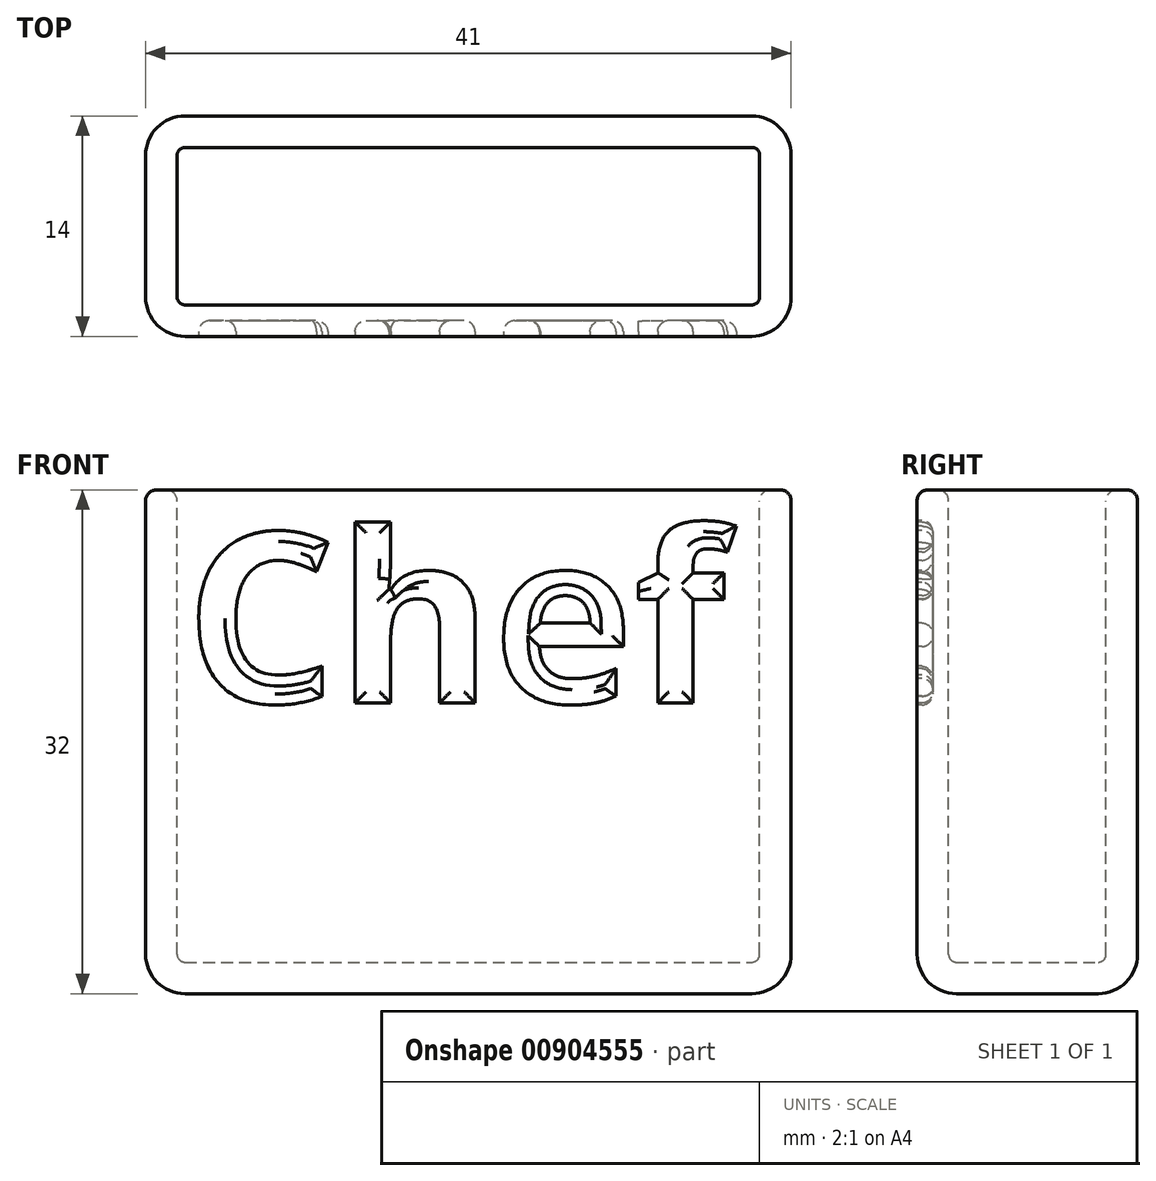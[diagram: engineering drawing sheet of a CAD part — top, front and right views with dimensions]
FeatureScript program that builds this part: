
annotation { "Feature Type Name" : "Feature", "Feature Type Description" : "" }
export const myFeature = defineFeature(function(context is Context, id is Id, definition is map)
    precondition{}
    {
        {
            var Q0;
            Q0=qCreatedBy(makeId("Top.planeOp"),FACE);
            var sketch = newSketch(context, id + "F0", { "sketchPlane" : qUnion([Q0])});
            skLineSegment(sketch, "E0.bottom", {"start": v(0, 0) * mm, "end": v(41, 0) * mm});
            skLineSegment(sketch, "E0.top", {"start": v(0, 14) * mm, "end": v(41, 14) * mm});
            skLineSegment(sketch, "E0.left", {"start": v(0, 0) * mm, "end": v(0, 14) * mm});
            skLineSegment(sketch, "E0.right", {"start": v(41, 0) * mm, "end": v(41, 14) * mm});
            skSolve(sketch);
        }
        {
            var Q0;
            Q0 = qSketchRegion(id + "F0", true);
            extrude(context, id + "F1", {"entities" : qUnion([Q0]), "depth" : 32 * mm, "offsetDistance" : 25 * mm});
        }
        {
            var Q0;
            Q0=makeQuery(id+"F1.opExtrude","SWEPT_EDGE",EDGE,{"disambiguationData":[OSD([sQuery(id+"F0.wireOp",EDGE,"E0.bottom"),sQuery(id+"F0.wireOp",EDGE,"E0.left")])]});
            var Q1;
            Q1=makeQuery(id+"F1.opExtrude","CAP_EDGE",EDGE,{"disambiguationData":[OSD([sQuery(id+"F0.wireOp",EDGE,"E0.bottom")])],"isStart":true});
            var Q2;
            Q2=makeQuery(id+"F1.opExtrude","SWEPT_EDGE",EDGE,{"disambiguationData":[OSD([sQuery(id+"F0.wireOp",EDGE,"E0.bottom"),sQuery(id+"F0.wireOp",EDGE,"E0.right")])]});
            var Q3;
            Q3=makeQuery(id+"F1.opExtrude","SWEPT_EDGE",EDGE,{"disambiguationData":[OSD([sQuery(id+"F0.wireOp",EDGE,"E0.top"),sQuery(id+"F0.wireOp",EDGE,"E0.right")])]});
            var Q4;
            Q4=makeQuery(id+"F1.opExtrude","SWEPT_EDGE",EDGE,{"disambiguationData":[OSD([sQuery(id+"F0.wireOp",EDGE,"E0.top"),sQuery(id+"F0.wireOp",EDGE,"E0.left")])]});
            var Q5;
            Q5=makeQuery(id+"F1.opExtrude","CAP_EDGE",EDGE,{"disambiguationData":[OSD([sQuery(id+"F0.wireOp",EDGE,"E0.top")])],"isStart":true});
            var Q6;
            Q6=makeQuery(id+"F1.opExtrude","CAP_EDGE",EDGE,{"disambiguationData":[OSD([sQuery(id+"F0.wireOp",EDGE,"E0.left")])],"isStart":true});
            var Q7;
            Q7=makeQuery(id+"F1.opExtrude","CAP_EDGE",EDGE,{"disambiguationData":[OSD([sQuery(id+"F0.wireOp",EDGE,"E0.right")])],"isStart":true});
            fillet(context, id + "F2", {"entities" : qUnion([Q0, Q1, Q2, Q3, Q4, Q5, Q6, Q7]), "radius" : 2.5 * mm, "tangentPropagation" : true, "allowEdgeOverflow" : false});
        }
        {
            var Q0;
            Q0=makeQuery(id+"F1.opExtrude","CAP_FACE",FACE,{"disambiguationData":[OSD([sQuery(id+"F0.wireOp",EDGE,"E0.bottom"),sQuery(id+"F0.wireOp",EDGE,"E0.top"),sQuery(id+"F0.wireOp",EDGE,"E0.left"),sQuery(id+"F0.wireOp",EDGE,"E0.right")])],"isStart":false});
            shell(context, id + "F3", {"entities" : qUnion([Q0]), "thickness" : 2 * mm});
        }
        {
            var Q0;
            Q0=makeQuery(id+"F1.opExtrude","CAP_FACE",FACE,{"disambiguationData":[OSD([sQuery(id+"F0.wireOp",EDGE,"E0.bottom"),sQuery(id+"F0.wireOp",EDGE,"E0.top"),sQuery(id+"F0.wireOp",EDGE,"E0.left"),sQuery(id+"F0.wireOp",EDGE,"E0.right")])],"isStart":false});
            fillet(context, id + "F4", {"entities" : qUnion([Q0]), "radius" : 0.7 * mm, "tangentPropagation" : true, "allowEdgeOverflow" : false});
        }
        {
            var Q0;
            Q0=makeQuery(id+"F1.opExtrude","SWEPT_FACE",FACE,{"disambiguationData":[OSD([sQuery(id+"F0.wireOp",EDGE,"E0.bottom")])]});
            var sketch = newSketch(context, id + "F5", { "sketchPlane" : qUnion([Q0])});
            skText(sketch, "E1", { "text": "Chef", "fontName": "OpenSans-Bold.ttf"});
            const initialGuessF5  = {"E1": [0.0025, 0.01848, 1, 0, 0.01088]};
            skSetInitialGuess(sketch, initialGuessF5);
            skSolve(sketch);
        }
        {
            var Q0;
            Q0=makeQuery(id+"F5.imprint","IMPRINT",FACE,{"disambiguationData":[TD([[makeQuery(id+"F5.imprint","IMPRINT",EDGE,{"derivedFrom":sQuery(id+"F5.wireOp",EDGE,"E1.sketch_text.stroke-0")}),-1.0]])]});
            var Q1;
            Q1=makeQuery(id+"F5.imprint","IMPRINT",FACE,{"disambiguationData":[TD([[makeQuery(id+"F5.imprint","IMPRINT",EDGE,{"derivedFrom":sQuery(id+"F5.wireOp",EDGE,"E1.sketch_text.stroke-15")}),-1.0]])]});
            var Q2;
            Q2 = qSketchRegion(id + "F5", true);
            extrude(context, id + "F6", {"entities" : qUnion([Q0, Q1, Q2]), "operationType" : NewBodyOperationType.REMOVE, "oppositeDirection" : true, "depth" : 1 * mm, "offsetDistance" : 25 * mm});
        }
        {
            var Q0;
            Q0=makeQuery(id+"F6.boolean.opBoolean","COPY",FACE,{"derivedFrom":makeQuery(id+"F6.opExtrude","CAP_FACE",FACE,{"disambiguationData":[OSD([sQuery(id+"F5.wireOp",EDGE,"E1.sketch_text.stroke-15"),sQuery(id+"F5.wireOp",EDGE,"E1.sketch_text.stroke-16"),sQuery(id+"F5.wireOp",EDGE,"E1.sketch_text.stroke-17"),sQuery(id+"F5.wireOp",EDGE,"E1.sketch_text.stroke-18"),sQuery(id+"F5.wireOp",EDGE,"E1.sketch_text.stroke-19"),sQuery(id+"F5.wireOp",EDGE,"E1.sketch_text.stroke-20"),sQuery(id+"F5.wireOp",EDGE,"E1.sketch_text.stroke-21"),sQuery(id+"F5.wireOp",EDGE,"E1.sketch_text.stroke-22"),sQuery(id+"F5.wireOp",EDGE,"E1.sketch_text.stroke-23"),sQuery(id+"F5.wireOp",EDGE,"E1.sketch_text.stroke-24"),sQuery(id+"F5.wireOp",EDGE,"E1.sketch_text.stroke-25"),sQuery(id+"F5.wireOp",EDGE,"E1.sketch_text.stroke-26"),sQuery(id+"F5.wireOp",EDGE,"E1.sketch_text.stroke-27"),sQuery(id+"F5.wireOp",EDGE,"E1.sketch_text.stroke-28"),sQuery(id+"F5.wireOp",EDGE,"E1.sketch_text.stroke-29"),sQuery(id+"F5.wireOp",EDGE,"E1.sketch_text.stroke-30"),sQuery(id+"F5.wireOp",EDGE,"E1.sketch_text.stroke-31")])],"isStart":false})});
            var Q1;
            Q1=makeQuery(id+"F6.boolean.opBoolean","COPY",FACE,{"derivedFrom":makeQuery(id+"F6.opExtrude","CAP_FACE",FACE,{"disambiguationData":[OSD([sQuery(id+"F5.wireOp",EDGE,"E1.sketch_text.stroke-0"),sQuery(id+"F5.wireOp",EDGE,"E1.sketch_text.stroke-1"),sQuery(id+"F5.wireOp",EDGE,"E1.sketch_text.stroke-2"),sQuery(id+"F5.wireOp",EDGE,"E1.sketch_text.stroke-3"),sQuery(id+"F5.wireOp",EDGE,"E1.sketch_text.stroke-4"),sQuery(id+"F5.wireOp",EDGE,"E1.sketch_text.stroke-5"),sQuery(id+"F5.wireOp",EDGE,"E1.sketch_text.stroke-6"),sQuery(id+"F5.wireOp",EDGE,"E1.sketch_text.stroke-7"),sQuery(id+"F5.wireOp",EDGE,"E1.sketch_text.stroke-8"),sQuery(id+"F5.wireOp",EDGE,"E1.sketch_text.stroke-9"),sQuery(id+"F5.wireOp",EDGE,"E1.sketch_text.stroke-10"),sQuery(id+"F5.wireOp",EDGE,"E1.sketch_text.stroke-11"),sQuery(id+"F5.wireOp",EDGE,"E1.sketch_text.stroke-12"),sQuery(id+"F5.wireOp",EDGE,"E1.sketch_text.stroke-13"),sQuery(id+"F5.wireOp",EDGE,"E1.sketch_text.stroke-14")])],"isStart":false})});
            var Q2;
            Q2=makeQuery(id+"F6.boolean.opBoolean","COPY",FACE,{"derivedFrom":makeQuery(id+"F6.opExtrude","CAP_FACE",FACE,{"disambiguationData":[OSD([sQuery(id+"F5.wireOp",EDGE,"E1.sketch_text.stroke-32"),sQuery(id+"F5.wireOp",EDGE,"E1.sketch_text.stroke-33"),sQuery(id+"F5.wireOp",EDGE,"E1.sketch_text.stroke-34"),sQuery(id+"F5.wireOp",EDGE,"E1.sketch_text.stroke-35"),sQuery(id+"F5.wireOp",EDGE,"E1.sketch_text.stroke-36"),sQuery(id+"F5.wireOp",EDGE,"E1.sketch_text.stroke-37"),sQuery(id+"F5.wireOp",EDGE,"E1.sketch_text.stroke-38"),sQuery(id+"F5.wireOp",EDGE,"E1.sketch_text.stroke-39"),sQuery(id+"F5.wireOp",EDGE,"E1.sketch_text.stroke-40"),sQuery(id+"F5.wireOp",EDGE,"E1.sketch_text.stroke-41"),sQuery(id+"F5.wireOp",EDGE,"E1.sketch_text.stroke-42"),sQuery(id+"F5.wireOp",EDGE,"E1.sketch_text.stroke-43"),sQuery(id+"F5.wireOp",EDGE,"E1.sketch_text.stroke-44"),sQuery(id+"F5.wireOp",EDGE,"E1.sketch_text.stroke-45"),sQuery(id+"F5.wireOp",EDGE,"E1.sketch_text.stroke-46"),sQuery(id+"F5.wireOp",EDGE,"E1.sketch_text.stroke-47"),sQuery(id+"F5.wireOp",EDGE,"E1.sketch_text.stroke-48"),sQuery(id+"F5.wireOp",EDGE,"E1.sketch_text.stroke-49"),sQuery(id+"F5.wireOp",EDGE,"E1.sketch_text.stroke-50"),sQuery(id+"F5.wireOp",EDGE,"E1.sketch_text.stroke-51")])],"isStart":false})});
            var Q3;
            Q3=makeQuery(id+"F6.boolean.opBoolean","COPY",FACE,{"derivedFrom":makeQuery(id+"F6.opExtrude","CAP_FACE",FACE,{"disambiguationData":[OSD([sQuery(id+"F5.wireOp",EDGE,"E1.sketch_text.stroke-52"),sQuery(id+"F5.wireOp",EDGE,"E1.sketch_text.stroke-53"),sQuery(id+"F5.wireOp",EDGE,"E1.sketch_text.stroke-54"),sQuery(id+"F5.wireOp",EDGE,"E1.sketch_text.stroke-55"),sQuery(id+"F5.wireOp",EDGE,"E1.sketch_text.stroke-56"),sQuery(id+"F5.wireOp",EDGE,"E1.sketch_text.stroke-57"),sQuery(id+"F5.wireOp",EDGE,"E1.sketch_text.stroke-58"),sQuery(id+"F5.wireOp",EDGE,"E1.sketch_text.stroke-59"),sQuery(id+"F5.wireOp",EDGE,"E1.sketch_text.stroke-60"),sQuery(id+"F5.wireOp",EDGE,"E1.sketch_text.stroke-61"),sQuery(id+"F5.wireOp",EDGE,"E1.sketch_text.stroke-62"),sQuery(id+"F5.wireOp",EDGE,"E1.sketch_text.stroke-63"),sQuery(id+"F5.wireOp",EDGE,"E1.sketch_text.stroke-64"),sQuery(id+"F5.wireOp",EDGE,"E1.sketch_text.stroke-65"),sQuery(id+"F5.wireOp",EDGE,"E1.sketch_text.stroke-66"),sQuery(id+"F5.wireOp",EDGE,"E1.sketch_text.stroke-67"),sQuery(id+"F5.wireOp",EDGE,"E1.sketch_text.stroke-68"),sQuery(id+"F5.wireOp",EDGE,"E1.sketch_text.stroke-69")])],"isStart":false})});
            fillet(context, id + "F7", {"entities" : qUnion([Q0, Q1, Q2, Q3]), "radius" : 0.7 * mm, "tangentPropagation" : true, "allowEdgeOverflow" : false});
        }
    });
